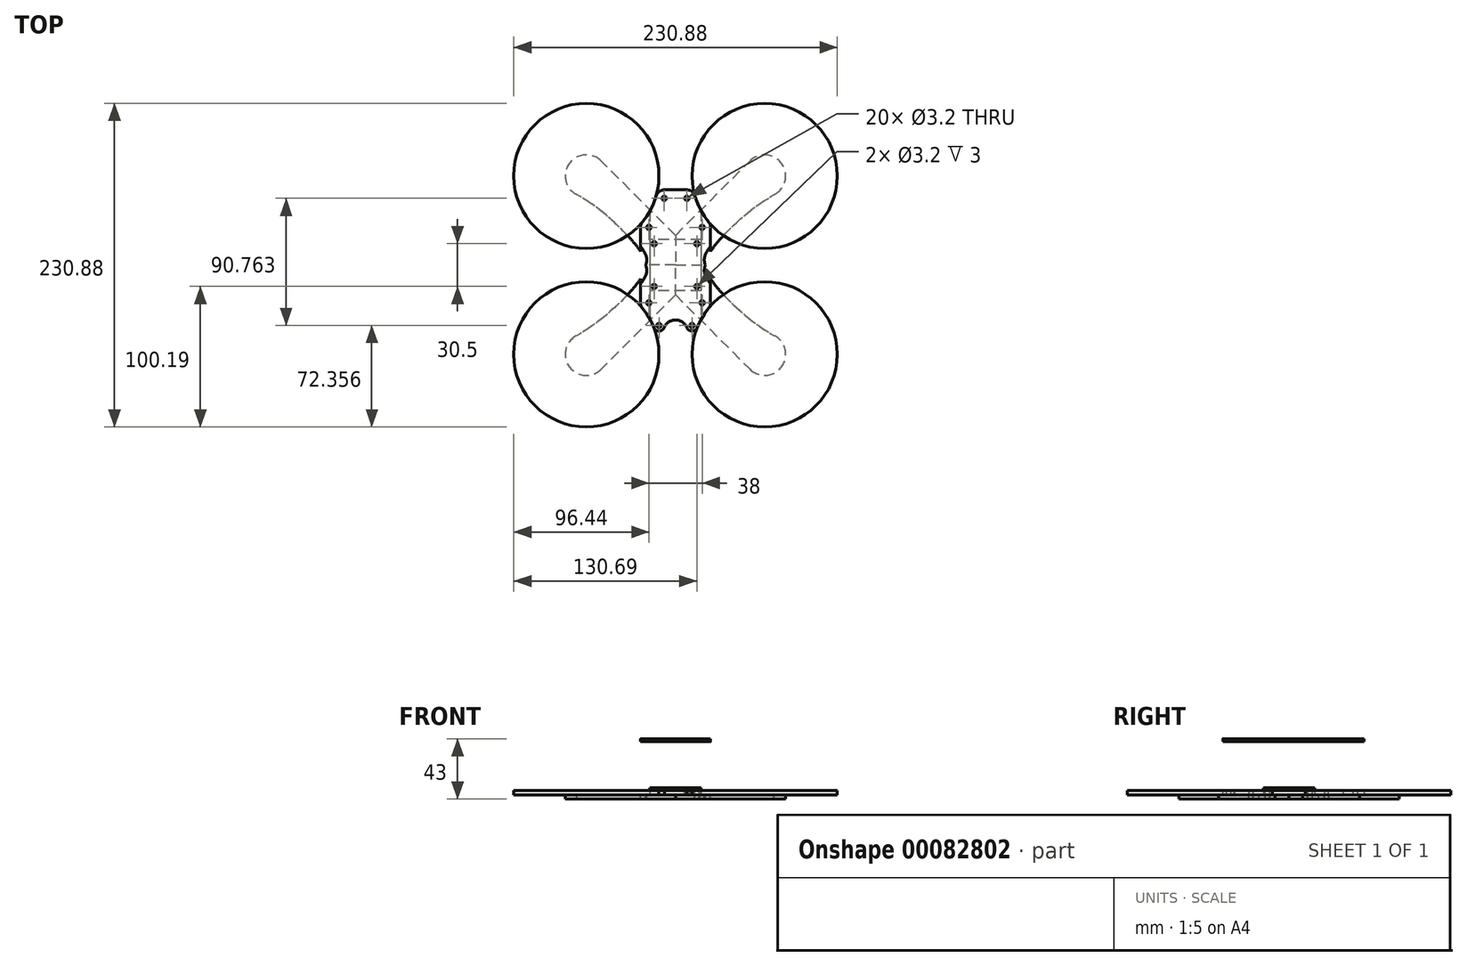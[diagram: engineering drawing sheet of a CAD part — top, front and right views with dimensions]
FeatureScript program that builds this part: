
annotation { "Feature Type Name" : "Feature", "Feature Type Description" : "" }
export const myFeature = defineFeature(function(context is Context, id is Id, definition is map)
    precondition{}
    {
        {
            var Q0;
            Q0=qCreatedBy(makeId("Top.planeOp"),FACE);
            var sketch = newSketch(context, id + "F0", { "sketchPlane" : qUnion([Q0])});
            skLineSegment(sketch, "E0", {"start": v(0, 0) * mm, "end": v(63.64, 63.64) * mm, "construction": true});
            skLineSegment(sketch, "E1", {"start": v(0, 0) * mm, "end": v(77.78, 77.78) * mm, "construction": true});
            skCircle(sketch, "E2", {"center": v(63.64, 63.64) * mm, "radius": 51.8 * mm});
            skCircle(sketch, "E3", {"center": v(77.78, 77.78) * mm, "radius": 64.5 * mm, "construction": true});
            skCircle(sketch, "E4.1.0", {"center": v(-77.78, 77.78) * mm, "radius": 64.5 * mm, "construction": true});
            skCircle(sketch, "E4.1.1", {"center": v(-63.64, 63.64) * mm, "radius": 51.8 * mm});
            skLineSegment(sketch, "E4.1.2", {"start": v(0, 0) * mm, "end": v(-77.78, 77.78) * mm, "construction": true});
            skLineSegment(sketch, "E4.1.3", {"start": v(0, 0) * mm, "end": v(-63.64, 63.64) * mm, "construction": true});
            skCircle(sketch, "E4.2.0", {"center": v(-77.78, -77.78) * mm, "radius": 64.5 * mm, "construction": true});
            skCircle(sketch, "E4.2.1", {"center": v(-63.64, -63.64) * mm, "radius": 51.8 * mm});
            skLineSegment(sketch, "E4.2.2", {"start": v(0, 0) * mm, "end": v(-77.78, -77.78) * mm, "construction": true});
            skLineSegment(sketch, "E4.2.3", {"start": v(0, 0) * mm, "end": v(-63.64, -63.64) * mm, "construction": true});
            skCircle(sketch, "E4.3.0", {"center": v(77.78, -77.78) * mm, "radius": 64.5 * mm, "construction": true});
            skCircle(sketch, "E4.3.1", {"center": v(63.64, -63.64) * mm, "radius": 51.8 * mm});
            skLineSegment(sketch, "E4.3.2", {"start": v(0, 0) * mm, "end": v(77.78, -77.78) * mm, "construction": true});
            skLineSegment(sketch, "E4.3.3", {"start": v(0, 0) * mm, "end": v(63.64, -63.64) * mm, "construction": true});
            skPoint(sketch, "E4.center", {"position": v(0, 0) * mm});
            skLineSegment(sketch, "E5.bottom", {"start": v(18.25, 38.68) * mm, "end": v(-18.25, 38.68) * mm});
            skLineSegment(sketch, "E5.top", {"start": v(18.25, -38.68) * mm, "end": v(-18.25, -38.68) * mm});
            skLineSegment(sketch, "E5.left", {"start": v(18.25, 38.68) * mm, "end": v(18.25, -38.68) * mm});
            skLineSegment(sketch, "E5.right", {"start": v(-18.25, 38.68) * mm, "end": v(-18.25, -38.68) * mm});
            skLineSegment(sketch, "E6.bottom", {"start": v(18.25, 18.25) * mm, "end": v(-18.25, 18.25) * mm});
            skLineSegment(sketch, "E6.top", {"start": v(18.25, -18.25) * mm, "end": v(-18.25, -18.25) * mm});
            skLineSegment(sketch, "E6.left", {"start": v(18.25, 18.25) * mm, "end": v(18.25, -18.25) * mm});
            skLineSegment(sketch, "E6.right", {"start": v(-18.25, 18.25) * mm, "end": v(-18.25, -18.25) * mm});
            skLineSegment(sketch, "E7", {"start": v(-32.57, 53.68) * mm, "end": v(33.13, 53.68) * mm});
            skLineSegment(sketch, "E8", {"start": v(-35.42, -53.68) * mm, "end": v(38.62, -53.68) * mm});
            skLineSegment(sketch, "E9", {"start": v(25, 67.02) * mm, "end": v(25, -83.76) * mm});
            skLineSegment(sketch, "E10.MirrorCS", {"start": v(-25, 67.02) * mm, "end": v(-25, -83.76) * mm});
            skSolve(sketch);
        }
        {
            var Q0;
            {var subQ0=sQuery(id+"F0.wireOp",EDGE,"E5.bottom");Q0=makeQuery(id+"F0.imprint","IMPRINT",FACE,{"disambiguationData":[TD([[makeQuery(id+"F0.imprint","IMPRINT",EDGE,{"derivedFrom":subQ0}),-1.0]])]});}
            var Q1;
            {var subQ0=sQuery(id+"F0.wireOp",EDGE,"E5.bottom");Q1=makeQuery(id+"F0.imprint","IMPRINT",FACE,{"disambiguationData":[TD([[makeQuery(id+"F0.imprint","IMPRINT",EDGE,{"derivedFrom":subQ0}),1.0]])]});}
            var Q2;
            Q2=makeQuery(id+"F0.imprint","IMPRINT",FACE,{"disambiguationData":[TD([[makeQuery(id+"F0.imprint","IMPRINT",EDGE,{"derivedFrom":sQuery(id+"F0.wireOp",EDGE,"E6.bottom")}),1.0]])]});
            var Q3;
            {var subQ0=sQuery(id+"F0.wireOp",EDGE,"E5.top");Q3=makeQuery(id+"F0.imprint","IMPRINT",FACE,{"disambiguationData":[TD([[makeQuery(id+"F0.imprint","IMPRINT",EDGE,{"derivedFrom":subQ0}),-1.0]])]});}
            var Q4;
            {var subQ0=sQuery(id+"F0.wireOp",EDGE,"E5.top");Q4=makeQuery(id+"F0.imprint","IMPRINT",FACE,{"disambiguationData":[TD([[makeQuery(id+"F0.imprint","IMPRINT",EDGE,{"derivedFrom":subQ0}),1.0]])]});}
            var Q5;
            {var subQ5=sQuery(id+"F0.wireOp",EDGE,"E6.right");Q5=makeQuery(id+"F0.imprint","IMPRINT",FACE,{"disambiguationData":[TD([[makeQuery(id+"F0.imprint","IMPRINT",EDGE,{"derivedFrom":subQ5}),-1.0]])]});}
            var Q6;
            {var subQ3=sQuery(id+"F0.wireOp",EDGE,"E6.left");Q6=makeQuery(id+"F0.imprint","IMPRINT",FACE,{"disambiguationData":[TD([[makeQuery(id+"F0.imprint","IMPRINT",EDGE,{"derivedFrom":subQ3}),1.0]])]});}
            extrude(context, id + "F1", {"entities" : qUnion([Q0, Q1, Q2, Q3, Q4, Q5, Q6]), "depth" : 3 * mm});
        }
        {
            var Q0;
            Q0=makeQuery(id+"F0.imprint","IMPRINT",FACE,{"disambiguationData":[TD([[makeQuery(id+"F0.imprint","IMPRINT",EDGE,{"derivedFrom":sQuery(id+"F0.wireOp",EDGE,"E6.bottom")}),1.0]])]});
            extrude(context, id + "F2", {"entities" : qUnion([Q0]), "depth" : 5 * mm});
        }
        {
            var Q0;
            {var subQ0=sQuery(id+"F0.wireOp",EDGE,"E10.MirrorCS");var subQ1=sQuery(id+"F0.wireOp",EDGE,"E4.1.1");var subQ2=makeQuery(id+"F0.imprint","INTERSECT",VERTEX,{"derivedFrom":[subQ1,subQ0]});Q0=makeQuery(id+"F0.imprint","IMPRINT",FACE,{"disambiguationData":[TD([[makeQuery(id+"F0.imprint","IMPRINT",EDGE,{"disambiguationData":[TD([[subQ2,1.0]])],"derivedFrom":subQ1}),1.0]])]});}
            var Q1;
            {var subQ0=sQuery(id+"F0.wireOp",EDGE,"E7");var subQ1=sQuery(id+"F0.wireOp",EDGE,"E2");var subQ2=makeQuery(id+"F0.imprint","INTERSECT",VERTEX,{"derivedFrom":[subQ1,subQ0]});Q1=makeQuery(id+"F0.imprint","IMPRINT",FACE,{"disambiguationData":[TD([[makeQuery(id+"F0.imprint","IMPRINT",EDGE,{"disambiguationData":[TD([[subQ2,1.0]])],"derivedFrom":subQ1}),1.0]])]});}
            var Q2;
            {var subQ0=sQuery(id+"F0.wireOp",EDGE,"E8");var subQ1=sQuery(id+"F0.wireOp",EDGE,"E4.2.1");var subQ2=makeQuery(id+"F0.imprint","INTERSECT",VERTEX,{"derivedFrom":[subQ1,subQ0]});Q2=makeQuery(id+"F0.imprint","IMPRINT",FACE,{"disambiguationData":[TD([[makeQuery(id+"F0.imprint","IMPRINT",EDGE,{"disambiguationData":[TD([[subQ2,1.0]])],"derivedFrom":subQ1}),1.0]])]});}
            var Q3;
            {var subQ0=sQuery(id+"F0.wireOp",EDGE,"E9");var subQ1=sQuery(id+"F0.wireOp",EDGE,"E4.3.1");var subQ2=makeQuery(id+"F0.imprint","INTERSECT",VERTEX,{"derivedFrom":[subQ1,subQ0]});Q3=makeQuery(id+"F0.imprint","IMPRINT",FACE,{"disambiguationData":[TD([[makeQuery(id+"F0.imprint","IMPRINT",EDGE,{"disambiguationData":[TD([[subQ2,1.0]])],"derivedFrom":subQ1}),1.0]])]});}
            var Q4;
            {var subQ2=sQuery(id+"F0.wireOp",EDGE,"E9");var subQ4=sQuery(id+"F0.wireOp",EDGE,"E8");var subQ6=makeQuery(id+"F0.imprint","INTERSECT",VERTEX,{"derivedFrom":[subQ4,subQ2]});Q4=makeQuery(id+"F0.imprint","IMPRINT",FACE,{"disambiguationData":[TD([[makeQuery(id+"F0.imprint","IMPRINT",EDGE,{"disambiguationData":[TD([[subQ6,1.0]])],"derivedFrom":subQ4}),1.0]])]});}
            var Q5;
            {var subQ2=sQuery(id+"F0.wireOp",EDGE,"E8");var subQ4=sQuery(id+"F0.wireOp",EDGE,"E10.MirrorCS");var subQ6=makeQuery(id+"F0.imprint","INTERSECT",VERTEX,{"derivedFrom":[subQ2,subQ4]});Q5=makeQuery(id+"F0.imprint","IMPRINT",FACE,{"disambiguationData":[TD([[makeQuery(id+"F0.imprint","IMPRINT",EDGE,{"disambiguationData":[TD([[subQ6,-1.0]])],"derivedFrom":subQ2}),1.0]])]});}
            var Q6;
            {var subQ2=sQuery(id+"F0.wireOp",EDGE,"E10.MirrorCS");var subQ4=sQuery(id+"F0.wireOp",EDGE,"E7");var subQ6=makeQuery(id+"F0.imprint","INTERSECT",VERTEX,{"derivedFrom":[subQ4,subQ2]});Q6=makeQuery(id+"F0.imprint","IMPRINT",FACE,{"disambiguationData":[TD([[makeQuery(id+"F0.imprint","IMPRINT",EDGE,{"disambiguationData":[TD([[subQ6,-1.0]])],"derivedFrom":subQ4}),-1.0]])]});}
            var Q7;
            {var subQ2=sQuery(id+"F0.wireOp",EDGE,"E7");var subQ4=sQuery(id+"F0.wireOp",EDGE,"E9");var subQ6=makeQuery(id+"F0.imprint","INTERSECT",VERTEX,{"derivedFrom":[subQ2,subQ4]});Q7=makeQuery(id+"F0.imprint","IMPRINT",FACE,{"disambiguationData":[TD([[makeQuery(id+"F0.imprint","IMPRINT",EDGE,{"disambiguationData":[TD([[subQ6,1.0]])],"derivedFrom":subQ2}),-1.0]])]});}
            extrude(context, id + "F3", {"entities" : qUnion([Q0, Q1, Q2, Q3, Q4, Q5, Q6, Q7]), "depth" : 3 * mm});
        }
        {
            var Q0;
            {var subQ0=sQuery(id+"F0.wireOp",EDGE,"E5.bottom");Q0=makeQuery(id+"F0.imprint","IMPRINT",FACE,{"disambiguationData":[TD([[makeQuery(id+"F0.imprint","IMPRINT",EDGE,{"derivedFrom":subQ0}),-1.0]])]});}
            var sketch = newSketch(context, id + "F4", { "sketchPlane" : qUnion([Q0])});
            skArc(sketch, "E11.0.0", {"start": v(-12.8, 53.68) * mm, "mid": v(-17.25, 40.59) * mm, "end": v(-25, 29.14) * mm, "construction": true});
            skLineSegment(sketch, "E11.0.1", {"start": v(-25, 29.14) * mm, "end": v(-25, -29.14) * mm, "construction": true});
            skArc(sketch, "E11.0.2", {"start": v(-25, -29.14) * mm, "mid": v(-17.25, -40.59) * mm, "end": v(-12.8, -53.68) * mm, "construction": true});
            skLineSegment(sketch, "E11.0.3", {"start": v(-12.8, -53.68) * mm, "end": v(12.8, -53.68) * mm, "construction": true});
            skArc(sketch, "E11.0.4", {"start": v(12.8, -53.68) * mm, "mid": v(17.25, -40.59) * mm, "end": v(25, -29.14) * mm, "construction": true});
            skLineSegment(sketch, "E11.0.5", {"start": v(25, -29.14) * mm, "end": v(25, 29.14) * mm, "construction": true});
            skArc(sketch, "E11.0.6", {"start": v(25, 29.14) * mm, "mid": v(17.25, 40.59) * mm, "end": v(12.8, 53.68) * mm, "construction": true});
            skLineSegment(sketch, "E11.0.7", {"start": v(12.8, 53.68) * mm, "end": v(-12.8, 53.68) * mm, "construction": true});
            skCircle(sketch, "E12", {"center": v(63.64, -63.64) * mm, "radius": 15 * mm, "construction": true});
            skLineSegment(sketch, "E13", {"start": v(98.26, -77.05) * mm, "end": v(21.21, 0) * mm});
            skLineSegment(sketch, "E14", {"start": v(0, -21.21) * mm, "end": v(70.57, -91.78) * mm});
            skLineSegment(sketch, "E15", {"start": v(0, -21.21) * mm, "end": v(0, 0) * mm});
            skLineSegment(sketch, "E16", {"start": v(0, 0) * mm, "end": v(21.21, 0) * mm});
            skArc(sketch, "E17", {"start": v(74.25, -53.03) * mm, "mid": v(74.25, -74.25) * mm, "end": v(53.03, -74.25) * mm});
            skSolve(sketch);
        }
        {
            var Q0;
            {var subQ1=sQuery(id+"F4.wireOp",EDGE,"E15");Q0=makeQuery(id+"F4.imprint","IMPRINT",FACE,{"disambiguationData":[TD([[makeQuery(id+"F4.imprint","IMPRINT",EDGE,{"derivedFrom":subQ1}),-1.0]])]});}
            extrude(context, id + "F5", {"entities" : qUnion([Q0]), "oppositeDirection" : true, "depth" : 3 * mm});
        }
        {
            var Q0;
            Q0=makeQuery(id+"F1.opExtrude","SWEPT_EDGE",EDGE,{"disambiguationData":[OSD([sQuery(id+"F0.wireOp",EDGE,"E4.3.1"),sQuery(id+"F0.wireOp",EDGE,"E9")])]});
            var Q1;
            Q1=makeQuery(id+"F1.opExtrude","SWEPT_EDGE",EDGE,{"disambiguationData":[OSD([sQuery(id+"F0.wireOp",EDGE,"E4.3.1"),sQuery(id+"F0.wireOp",EDGE,"E8")])]});
            var Q2;
            Q2=makeQuery(id+"F1.opExtrude","SWEPT_EDGE",EDGE,{"disambiguationData":[OSD([sQuery(id+"F0.wireOp",EDGE,"E2"),sQuery(id+"F0.wireOp",EDGE,"E9")])]});
            var Q3;
            Q3=makeQuery(id+"F1.opExtrude","SWEPT_EDGE",EDGE,{"disambiguationData":[OSD([sQuery(id+"F0.wireOp",EDGE,"E2"),sQuery(id+"F0.wireOp",EDGE,"E7")])]});
            var Q4;
            Q4=makeQuery(id+"F1.opExtrude","SWEPT_EDGE",EDGE,{"disambiguationData":[OSD([sQuery(id+"F0.wireOp",EDGE,"E4.1.1"),sQuery(id+"F0.wireOp",EDGE,"E7")])]});
            var Q5;
            Q5=makeQuery(id+"F1.opExtrude","SWEPT_EDGE",EDGE,{"disambiguationData":[OSD([sQuery(id+"F0.wireOp",EDGE,"E4.1.1"),sQuery(id+"F0.wireOp",EDGE,"E10.MirrorCS")])]});
            var Q6;
            Q6=makeQuery(id+"F1.opExtrude","SWEPT_EDGE",EDGE,{"disambiguationData":[OSD([sQuery(id+"F0.wireOp",EDGE,"E4.2.1"),sQuery(id+"F0.wireOp",EDGE,"E10.MirrorCS")])]});
            var Q7;
            Q7=makeQuery(id+"F1.opExtrude","SWEPT_EDGE",EDGE,{"disambiguationData":[OSD([sQuery(id+"F0.wireOp",EDGE,"E4.2.1"),sQuery(id+"F0.wireOp",EDGE,"E8")])]});
            fillet(context, id + "F6", {"entities" : qUnion([Q0, Q1, Q2, Q3, Q4, Q5, Q6, Q7]), "radius" : 6 * mm, "allowEdgeOverflow" : false});
        }
        {
            var Q0;
            Q0=makeQuery(id+"F5.opExtrude","CAP_FACE",FACE,{"disambiguationData":[OSD([sQuery(id+"F4.wireOp",EDGE,"E13"),sQuery(id+"F4.wireOp",EDGE,"E14"),sQuery(id+"F4.wireOp",EDGE,"E15"),sQuery(id+"F4.wireOp",EDGE,"E16"),sQuery(id+"F4.wireOp",EDGE,"E17")])],"isStart":true});
            var sketch = newSketch(context, id + "F7", { "sketchPlane" : qUnion([Q0])});
            skArc(sketch, "E18.0.0", {"start": v(53.03, -74.25) * mm, "mid": v(74.25, -74.25) * mm, "end": v(74.25, -53.03) * mm});
            skLineSegment(sketch, "E18.0.1", {"start": v(74.25, -53.03) * mm, "end": v(21.21, 0) * mm});
            skLineSegment(sketch, "E18.0.2", {"start": v(21.21, 0) * mm, "end": v(0, 0) * mm});
            skLineSegment(sketch, "E18.0.3", {"start": v(0, 0) * mm, "end": v(0, -21.21) * mm});
            skLineSegment(sketch, "E18.0.4", {"start": v(0, -21.21) * mm, "end": v(53.03, -74.25) * mm});
            skLineSegment(sketch, "E19.0", {"start": v(25, 67.02) * mm, "end": v(25, -83.76) * mm});
            skCircle(sketch, "E20", {"center": v(63.64, -63.64) * mm, "radius": 15 * mm});
            skFitSpline(sketch, "E21", {"points": [v(21.21, 0) * mm, v(40.17, -27.1) * mm, v(70.4, -50.25) * mm], "startDerivative": vector(0, -45.66) * mm, "endDerivative": vector(63.78, -35.61) * mm});
            skArc(sketch, "E22.0.0", {"start": v(23.63, 30.73) * mm, "mid": v(17.8, 39.53) * mm, "end": v(13.85, 49.34) * mm});
            skArc(sketch, "E22.0.1", {"start": v(13.85, 49.34) * mm, "mid": v(11.7, 52.47) * mm, "end": v(8.09, 53.68) * mm});
            skLineSegment(sketch, "E22.0.2", {"start": v(8.09, 53.68) * mm, "end": v(-8.09, 53.68) * mm});
            skArc(sketch, "E22.0.3", {"start": v(-8.09, 53.68) * mm, "mid": v(-11.7, 52.47) * mm, "end": v(-13.85, 49.34) * mm});
            skArc(sketch, "E22.0.4", {"start": v(-13.85, 49.34) * mm, "mid": v(-17.8, 39.53) * mm, "end": v(-23.63, 30.73) * mm});
            skArc(sketch, "E22.0.5", {"start": v(-23.63, 30.73) * mm, "mid": v(-24.65, 28.95) * mm, "end": v(-25, 26.92) * mm});
            skLineSegment(sketch, "E22.0.6", {"start": v(-25, 26.92) * mm, "end": v(-25, -26.92) * mm});
            skArc(sketch, "E22.0.7", {"start": v(-25, -26.92) * mm, "mid": v(-24.65, -28.95) * mm, "end": v(-23.63, -30.73) * mm});
            skArc(sketch, "E22.0.8", {"start": v(-23.63, -30.73) * mm, "mid": v(-17.8, -39.53) * mm, "end": v(-13.85, -49.34) * mm});
            skArc(sketch, "E22.0.9", {"start": v(-13.85, -49.34) * mm, "mid": v(-11.7, -52.47) * mm, "end": v(-8.09, -53.68) * mm});
            skLineSegment(sketch, "E22.0.10", {"start": v(-8.09, -53.68) * mm, "end": v(8.09, -53.68) * mm});
            skArc(sketch, "E22.0.11", {"start": v(8.09, -53.68) * mm, "mid": v(11.7, -52.47) * mm, "end": v(13.85, -49.34) * mm});
            skArc(sketch, "E22.0.12", {"start": v(13.85, -49.34) * mm, "mid": v(17.8, -39.53) * mm, "end": v(23.63, -30.73) * mm});
            skArc(sketch, "E22.0.13", {"start": v(23.63, -30.73) * mm, "mid": v(24.65, -28.95) * mm, "end": v(25, -26.92) * mm});
            skLineSegment(sketch, "E22.0.14", {"start": v(25, -26.92) * mm, "end": v(25, 26.92) * mm});
            skArc(sketch, "E22.0.15", {"start": v(25, 26.92) * mm, "mid": v(24.65, 28.95) * mm, "end": v(23.63, 30.73) * mm});
            skSolve(sketch);
        }
        {
            var Q0;
            {var subQ0=sQuery(id+"F7.wireOp",EDGE,"E20");var subQ1=sQuery(id+"F7.wireOp",EDGE,"E18.0.1");var subQ2=makeQuery(id+"F7.imprint","INTERSECT",VERTEX,{"derivedFrom":[subQ1,subQ0]});Q0=makeQuery(id+"F7.imprint","IMPRINT",FACE,{"disambiguationData":[TD([[makeQuery(id+"F7.imprint","IMPRINT",EDGE,{"disambiguationData":[TD([[subQ2,-1.0]])],"derivedFrom":subQ1}),1.0]])]});}
            var Q1;
            {var subQ1=sQuery(id+"F7.wireOp",EDGE,"E18.0.1");var subQ3=sQuery(id+"F7.wireOp",EDGE,"E22.0.14");var subQ4=makeQuery(id+"F7.imprint","INTERSECT",VERTEX,{"derivedFrom":[subQ1,subQ3]});Q1=makeQuery(id+"F7.imprint","IMPRINT",FACE,{"disambiguationData":[TD([[makeQuery(id+"F7.imprint","IMPRINT",EDGE,{"disambiguationData":[TD([[subQ4,1.0]])],"derivedFrom":subQ3}),1.0]])]});}
            extrude(context, id + "F8", {"entities" : qUnion([Q0, Q1]), "operationType" : NewBodyOperationType.REMOVE, "endBound" : BoundingType.THROUGH_ALL, "oppositeDirection" : true, "depth" : 25 * mm});
        }
        {
            var Q0;
            Q0=makeQuery(id+"F5.opExtrude","SWEPT_BODY",BODY,{"disambiguationData":[OSD([sQuery(id+"F4.wireOp",EDGE,"E13"),sQuery(id+"F4.wireOp",EDGE,"E14"),sQuery(id+"F4.wireOp",EDGE,"E15"),sQuery(id+"F4.wireOp",EDGE,"E16"),sQuery(id+"F4.wireOp",EDGE,"E17")])]});
            var Q1;
            Q1=makeQuery(id+"F5.opExtrude","SWEPT_EDGE",EDGE,{"disambiguationData":[OSD([sQuery(id+"F4.wireOp",EDGE,"E15"),sQuery(id+"F4.wireOp",EDGE,"E16")])]});
            circularPattern(context, id + "F9", {"entities" : qUnion([Q0]), "axis" : qUnion([Q1]), "angle" : 180 * degree, "instanceCount" : 2});
        }
        {
            var Q0;
            Q0=makeQuery(id+"F9.opPattern","COPY",BODY,{"derivedFrom":makeQuery(id+"F5.opExtrude","SWEPT_BODY",BODY,{"disambiguationData":[OSD([sQuery(id+"F4.wireOp",EDGE,"E13"),sQuery(id+"F4.wireOp",EDGE,"E14"),sQuery(id+"F4.wireOp",EDGE,"E15"),sQuery(id+"F4.wireOp",EDGE,"E16"),sQuery(id+"F4.wireOp",EDGE,"E17")])]}),"instanceName":"1"});
            var Q1;
            Q1=makeQuery(id+"F5.opExtrude","SWEPT_BODY",BODY,{"disambiguationData":[OSD([sQuery(id+"F4.wireOp",EDGE,"E13"),sQuery(id+"F4.wireOp",EDGE,"E14"),sQuery(id+"F4.wireOp",EDGE,"E15"),sQuery(id+"F4.wireOp",EDGE,"E16"),sQuery(id+"F4.wireOp",EDGE,"E17")])]});
            var Q2;
            Q2=qCreatedBy(makeId("Right.planeOp"),FACE);
            mirror(context, id + "F10", {"entities" : qUnion([Q0, Q1]), "mirrorPlane" : qUnion([Q2])});
        }
        {
            var Q0;
            Q0=makeQuery(id+"F1.opExtrude","CAP_FACE",FACE,{"disambiguationData":[OSD([sQuery(id+"F0.wireOp",EDGE,"E2"),sQuery(id+"F0.wireOp",EDGE,"E4.1.1"),sQuery(id+"F0.wireOp",EDGE,"E4.2.1"),sQuery(id+"F0.wireOp",EDGE,"E4.3.1"),sQuery(id+"F0.wireOp",EDGE,"E7"),sQuery(id+"F0.wireOp",EDGE,"E8"),sQuery(id+"F0.wireOp",EDGE,"E9"),sQuery(id+"F0.wireOp",EDGE,"E10.MirrorCS")])],"isStart":false});
            var sketch = newSketch(context, id + "F11", { "sketchPlane" : qUnion([Q0])});
            skFitSpline(sketch, "E23.0", {"points": [v(21.21, 0) * mm, v(21.21, -7.34) * mm, v(41.38, -29.78) * mm, v(59.4, -44.1) * mm, v(70.4, -50.25) * mm]});
            skFitSpline(sketch, "E24.0", {"points": [v(21.21, 0) * mm, v(21.21, 7.34) * mm, v(41.38, 29.78) * mm, v(59.4, 44.1) * mm, v(70.4, 50.25) * mm]});
            skLineSegment(sketch, "E25.0", {"start": v(25, 26.92) * mm, "end": v(25, -26.92) * mm});
            skFitSpline(sketch, "E26.0", {"points": [v(-21.21, 0) * mm, v(-21.21, 7.34) * mm, v(-41.38, 29.78) * mm, v(-59.4, 44.1) * mm, v(-70.4, 50.25) * mm]});
            skLineSegment(sketch, "E27.0", {"start": v(-25, 26.92) * mm, "end": v(-25, -26.92) * mm});
            skFitSpline(sketch, "E28.0", {"points": [v(-21.21, 0) * mm, v(-21.21, -7.34) * mm, v(-41.38, -29.78) * mm, v(-59.4, -44.1) * mm, v(-70.4, -50.25) * mm]});
            skSolve(sketch);
        }
        {
            var Q0;
            {var subQ0=sQuery(id+"F11.wireOp",EDGE,"E28.0");var subQ1=sQuery(id+"F11.wireOp",EDGE,"E26.0");var subQ2=makeQuery(id+"F11.imprint","INTERSECT",VERTEX,{"derivedFrom":[subQ1,subQ0]});Q0=makeQuery(id+"F11.imprint","IMPRINT",FACE,{"disambiguationData":[TD([[makeQuery(id+"F11.imprint","IMPRINT",EDGE,{"disambiguationData":[TD([[subQ2,-1.0]])],"derivedFrom":subQ1}),1.0]])]});}
            var Q1;
            {var subQ0=sQuery(id+"F11.wireOp",EDGE,"E24.0");var subQ1=sQuery(id+"F11.wireOp",EDGE,"E23.0");var subQ2=makeQuery(id+"F11.imprint","INTERSECT",VERTEX,{"derivedFrom":[subQ1,subQ0]});Q1=makeQuery(id+"F11.imprint","IMPRINT",FACE,{"disambiguationData":[TD([[makeQuery(id+"F11.imprint","IMPRINT",EDGE,{"disambiguationData":[TD([[subQ2,-1.0]])],"derivedFrom":subQ1}),1.0]])]});}
            extrude(context, id + "F12", {"entities" : qUnion([Q0, Q1]), "operationType" : NewBodyOperationType.REMOVE, "endBound" : BoundingType.THROUGH_ALL, "oppositeDirection" : true, "depth" : 25 * mm});
        }
        {
            var Q0;
            Q0=makeQuery(id+"F1.opExtrude","CAP_FACE",FACE,{"disambiguationData":[OSD([sQuery(id+"F0.wireOp",EDGE,"E2"),sQuery(id+"F0.wireOp",EDGE,"E4.1.1"),sQuery(id+"F0.wireOp",EDGE,"E4.2.1"),sQuery(id+"F0.wireOp",EDGE,"E4.3.1"),sQuery(id+"F0.wireOp",EDGE,"E7"),sQuery(id+"F0.wireOp",EDGE,"E8"),sQuery(id+"F0.wireOp",EDGE,"E9"),sQuery(id+"F0.wireOp",EDGE,"E10.MirrorCS")])],"isStart":false});
            cPlane(context, id + "F13", {"entities" : qUnion([Q0]), "cplaneType" : CPlaneType.OFFSET, "offset" : 35 * mm, "width" : 150 * mm, "height" : 150 * mm});
        }
        {
            var Q0;
            Q0=makeQuery(id+"F1.opExtrude","CAP_FACE",FACE,{"disambiguationData":[OSD([sQuery(id+"F0.wireOp",EDGE,"E2"),sQuery(id+"F0.wireOp",EDGE,"E4.1.1"),sQuery(id+"F0.wireOp",EDGE,"E4.2.1"),sQuery(id+"F0.wireOp",EDGE,"E4.3.1"),sQuery(id+"F0.wireOp",EDGE,"E7"),sQuery(id+"F0.wireOp",EDGE,"E8"),sQuery(id+"F0.wireOp",EDGE,"E9"),sQuery(id+"F0.wireOp",EDGE,"E10.MirrorCS")])],"isStart":false});
            var sketch = newSketch(context, id + "F14", { "sketchPlane" : qUnion([Q0])});
            skFitSpline(sketch, "E29.0.0", {"points": [v(70.4, -50.25) * mm, v(59.4, -44.1) * mm, v(41.38, -29.78) * mm, v(21.21, -7.34) * mm, v(21.21, 0) * mm], "construction": true});
            skFitSpline(sketch, "E29.0.1", {"points": [v(21.21, 0) * mm, v(21.21, 7.34) * mm, v(41.38, 29.78) * mm, v(59.4, 44.1) * mm, v(70.4, 50.25) * mm], "construction": true});
            skLineSegment(sketch, "E29.0.2", {"start": v(25, 9.8) * mm, "end": v(25, 26.92) * mm, "construction": true});
            skArc(sketch, "E29.0.3", {"start": v(25, 26.92) * mm, "mid": v(24.65, 28.95) * mm, "end": v(23.63, 30.73) * mm, "construction": true});
            skArc(sketch, "E29.0.4", {"start": v(23.63, 30.73) * mm, "mid": v(17.8, 39.53) * mm, "end": v(13.85, 49.34) * mm, "construction": true});
            skArc(sketch, "E29.0.5", {"start": v(13.85, 49.34) * mm, "mid": v(11.7, 52.47) * mm, "end": v(8.09, 53.68) * mm, "construction": true});
            skLineSegment(sketch, "E29.0.6", {"start": v(8.09, 53.68) * mm, "end": v(-8.09, 53.68) * mm, "construction": true});
            skArc(sketch, "E29.0.7", {"start": v(-8.09, 53.68) * mm, "mid": v(-11.7, 52.47) * mm, "end": v(-13.85, 49.34) * mm, "construction": true});
            skArc(sketch, "E29.0.8", {"start": v(-13.85, 49.34) * mm, "mid": v(-17.8, 39.53) * mm, "end": v(-23.63, 30.73) * mm, "construction": true});
            skArc(sketch, "E29.0.9", {"start": v(-23.63, 30.73) * mm, "mid": v(-24.65, 28.95) * mm, "end": v(-25, 26.92) * mm, "construction": true});
            skLineSegment(sketch, "E29.0.10", {"start": v(-25, 26.92) * mm, "end": v(-25, 9.8) * mm, "construction": true});
            skFitSpline(sketch, "E29.0.11", {"points": [v(-70.4, 50.25) * mm, v(-59.4, 44.1) * mm, v(-41.38, 29.78) * mm, v(-21.21, 7.34) * mm, v(-21.21, 0) * mm], "construction": true});
            skFitSpline(sketch, "E29.0.12", {"points": [v(-21.21, 0) * mm, v(-21.21, -7.34) * mm, v(-41.38, -29.78) * mm, v(-59.4, -44.1) * mm, v(-70.4, -50.25) * mm], "construction": true});
            skLineSegment(sketch, "E29.0.13", {"start": v(-25, -9.8) * mm, "end": v(-25, -26.92) * mm, "construction": true});
            skArc(sketch, "E29.0.14", {"start": v(-25, -26.92) * mm, "mid": v(-24.65, -28.95) * mm, "end": v(-23.63, -30.73) * mm, "construction": true});
            skArc(sketch, "E29.0.15", {"start": v(-23.63, -30.73) * mm, "mid": v(-17.8, -39.53) * mm, "end": v(-13.85, -49.34) * mm, "construction": true});
            skArc(sketch, "E29.0.16", {"start": v(-13.85, -49.34) * mm, "mid": v(-11.7, -52.47) * mm, "end": v(-8.09, -53.68) * mm, "construction": true});
            skLineSegment(sketch, "E29.0.17", {"start": v(-8.09, -53.68) * mm, "end": v(8.09, -53.68) * mm, "construction": true});
            skArc(sketch, "E29.0.18", {"start": v(8.09, -53.68) * mm, "mid": v(11.7, -52.47) * mm, "end": v(13.85, -49.34) * mm, "construction": true});
            skArc(sketch, "E29.0.19", {"start": v(13.85, -49.34) * mm, "mid": v(17.8, -39.53) * mm, "end": v(23.63, -30.73) * mm, "construction": true});
            skArc(sketch, "E29.0.20", {"start": v(23.63, -30.73) * mm, "mid": v(24.65, -28.95) * mm, "end": v(25, -26.92) * mm, "construction": true});
            skLineSegment(sketch, "E29.0.21", {"start": v(25, -26.92) * mm, "end": v(25, -9.8) * mm, "construction": true});
            skCircle(sketch, "E30", {"center": v(19, 26.92) * mm, "radius": 1.6 * mm});
            skCircle(sketch, "E31", {"center": v(19, -26.92) * mm, "radius": 1.6 * mm});
            skCircle(sketch, "E32", {"center": v(8.09, 47.68) * mm, "radius": 1.6 * mm});
            skCircle(sketch, "E33", {"center": v(15.25, 15.25) * mm, "radius": 1.6 * mm});
            skCircle(sketch, "E34", {"center": v(15.25, -15.25) * mm, "radius": 1.6 * mm});
            skCircle(sketch, "E35", {"center": v(11.76, -43.08) * mm, "radius": 1.6 * mm});
            skSolve(sketch);
        }
        {
            var Q0;
            Q0 = qSketchRegion(id + "F14", true);
            extrude(context, id + "F15", {"entities" : qUnion([Q0]), "operationType" : NewBodyOperationType.REMOVE, "endBound" : BoundingType.THROUGH_ALL, "oppositeDirection" : true, "depth" : 25 * mm});
        }
        {
            var Q0;
            Q0=qCreatedBy(id+"F13.planeOp",FACE);
            var sketch = newSketch(context, id + "F16", { "sketchPlane" : qUnion([Q0])});
            skFitSpline(sketch, "E36.0.0", {"points": [v(70.4, -50.25) * mm, v(59.4, -44.1) * mm, v(41.38, -29.78) * mm, v(21.21, -7.34) * mm, v(21.21, 0) * mm]});
            skFitSpline(sketch, "E36.0.1", {"points": [v(21.21, 0) * mm, v(21.21, 7.34) * mm, v(41.38, 29.78) * mm, v(59.4, 44.1) * mm, v(70.4, 50.25) * mm]});
            skLineSegment(sketch, "E36.0.2", {"start": v(25, 9.8) * mm, "end": v(25, 26.92) * mm});
            skArc(sketch, "E36.0.3", {"start": v(25, 26.92) * mm, "mid": v(24.65, 28.95) * mm, "end": v(23.63, 30.73) * mm});
            skArc(sketch, "E36.0.4", {"start": v(23.63, 30.73) * mm, "mid": v(17.8, 39.53) * mm, "end": v(13.85, 49.34) * mm});
            skArc(sketch, "E36.0.5", {"start": v(13.85, 49.34) * mm, "mid": v(11.7, 52.47) * mm, "end": v(8.09, 53.68) * mm});
            skLineSegment(sketch, "E36.0.6", {"start": v(8.09, 53.68) * mm, "end": v(-8.09, 53.68) * mm});
            skArc(sketch, "E36.0.7", {"start": v(-8.09, 53.68) * mm, "mid": v(-11.7, 52.47) * mm, "end": v(-13.85, 49.34) * mm});
            skArc(sketch, "E36.0.8", {"start": v(-13.85, 49.34) * mm, "mid": v(-17.8, 39.53) * mm, "end": v(-23.63, 30.73) * mm});
            skArc(sketch, "E36.0.9", {"start": v(-23.63, 30.73) * mm, "mid": v(-24.65, 28.95) * mm, "end": v(-25, 26.92) * mm});
            skLineSegment(sketch, "E36.0.10", {"start": v(-25, 26.92) * mm, "end": v(-25, 9.8) * mm});
            skFitSpline(sketch, "E36.0.11", {"points": [v(-70.4, 50.25) * mm, v(-59.4, 44.1) * mm, v(-41.38, 29.78) * mm, v(-21.21, 7.34) * mm, v(-21.21, 0) * mm]});
            skFitSpline(sketch, "E36.0.12", {"points": [v(-21.21, 0) * mm, v(-21.21, -7.34) * mm, v(-41.38, -29.78) * mm, v(-59.4, -44.1) * mm, v(-70.4, -50.25) * mm]});
            skLineSegment(sketch, "E36.0.13", {"start": v(-25, -9.8) * mm, "end": v(-25, -26.92) * mm});
            skArc(sketch, "E36.0.14", {"start": v(-25, -26.92) * mm, "mid": v(-24.65, -28.95) * mm, "end": v(-23.63, -30.73) * mm});
            skArc(sketch, "E36.0.15", {"start": v(-23.63, -30.73) * mm, "mid": v(-17.8, -39.53) * mm, "end": v(-13.85, -49.34) * mm});
            skArc(sketch, "E36.0.16", {"start": v(-13.85, -49.34) * mm, "mid": v(-11.7, -52.47) * mm, "end": v(-8.09, -53.68) * mm});
            skLineSegment(sketch, "E36.0.17", {"start": v(-8.09, -53.68) * mm, "end": v(8.09, -53.68) * mm});
            skArc(sketch, "E36.0.18", {"start": v(8.09, -53.68) * mm, "mid": v(11.7, -52.47) * mm, "end": v(13.85, -49.34) * mm});
            skArc(sketch, "E36.0.19", {"start": v(13.85, -49.34) * mm, "mid": v(17.8, -39.53) * mm, "end": v(23.63, -30.73) * mm});
            skArc(sketch, "E36.0.20", {"start": v(23.63, -30.73) * mm, "mid": v(24.65, -28.95) * mm, "end": v(25, -26.92) * mm});
            skLineSegment(sketch, "E36.0.21", {"start": v(25, -26.92) * mm, "end": v(25, -9.8) * mm});
            skCircle(sketch, "E37.0", {"center": v(-8.09, 47.68) * mm, "radius": 1.6 * mm});
            skCircle(sketch, "E38.0", {"center": v(8.09, 47.68) * mm, "radius": 1.6 * mm});
            skCircle(sketch, "E39.0", {"center": v(-19, 26.92) * mm, "radius": 1.6 * mm});
            skCircle(sketch, "E40.0", {"center": v(19, 26.92) * mm, "radius": 1.6 * mm});
            skCircle(sketch, "E41.0", {"center": v(15.25, 15.25) * mm, "radius": 1.6 * mm});
            skCircle(sketch, "E42.0", {"center": v(-15.25, 15.25) * mm, "radius": 1.6 * mm});
            skCircle(sketch, "E43.0", {"center": v(-15.25, -15.25) * mm, "radius": 1.6 * mm});
            skCircle(sketch, "E44.0", {"center": v(15.25, -15.25) * mm, "radius": 1.6 * mm});
            skCircle(sketch, "E45.0", {"center": v(19, -26.92) * mm, "radius": 1.6 * mm});
            skCircle(sketch, "E46.0", {"center": v(11.76, -43.08) * mm, "radius": 1.6 * mm});
            skCircle(sketch, "E47.0", {"center": v(-11.76, -43.08) * mm, "radius": 1.6 * mm});
            skCircle(sketch, "E48.0", {"center": v(-19, -26.92) * mm, "radius": 1.6 * mm});
            skSolve(sketch);
        }
        {
            var Q0;
            Q0=makeQuery(id+"F16.imprint","IMPRINT",FACE,{"disambiguationData":[TD([[makeQuery(id+"F16.imprint","IMPRINT",EDGE,{"derivedFrom":sQuery(id+"F16.wireOp",EDGE,"E36.0.0")}),1.0]])]});
            extrude(context, id + "F17", {"entities" : qUnion([Q0]), "depth" : 2 * mm});
        }
        {
            var Q0;
            Q0=makeQuery(id+"F3.opExtrude","CAP_FACE",FACE,{"disambiguationData":[OSD([sQuery(id+"F0.wireOp",EDGE,"E4.3.1")])],"isStart":false});
            var sketch = newSketch(context, id + "F18", { "sketchPlane" : qUnion([Q0])});
            skLineSegment(sketch, "E49.0.0", {"start": v(25, -26.92) * mm, "end": v(25, -9.8) * mm});
            skFitSpline(sketch, "E49.0.1", {"points": [v(70.4, -50.25) * mm, v(59.4, -44.1) * mm, v(41.38, -29.78) * mm, v(21.21, -7.34) * mm, v(21.21, 0) * mm]});
            skFitSpline(sketch, "E49.0.2", {"points": [v(21.21, 0) * mm, v(21.21, 7.34) * mm, v(41.38, 29.78) * mm, v(59.4, 44.1) * mm, v(70.4, 50.25) * mm]});
            skLineSegment(sketch, "E49.0.3", {"start": v(25, 9.8) * mm, "end": v(25, 26.92) * mm});
            skArc(sketch, "E49.0.4", {"start": v(25, 26.92) * mm, "mid": v(24.65, 28.95) * mm, "end": v(23.63, 30.73) * mm});
            skArc(sketch, "E49.0.5", {"start": v(23.63, 30.73) * mm, "mid": v(17.8, 39.53) * mm, "end": v(13.85, 49.34) * mm});
            skArc(sketch, "E49.0.6", {"start": v(13.85, 49.34) * mm, "mid": v(11.7, 52.47) * mm, "end": v(8.09, 53.68) * mm});
            skLineSegment(sketch, "E49.0.7", {"start": v(8.09, 53.68) * mm, "end": v(-8.09, 53.68) * mm});
            skArc(sketch, "E49.0.8", {"start": v(-8.09, 53.68) * mm, "mid": v(-11.7, 52.47) * mm, "end": v(-13.85, 49.34) * mm});
            skArc(sketch, "E49.0.9", {"start": v(-13.85, 49.34) * mm, "mid": v(-17.8, 39.53) * mm, "end": v(-23.63, 30.73) * mm});
            skArc(sketch, "E49.0.10", {"start": v(-23.63, 30.73) * mm, "mid": v(-24.65, 28.95) * mm, "end": v(-25, 26.92) * mm});
            skLineSegment(sketch, "E49.0.11", {"start": v(-25, 26.92) * mm, "end": v(-25, 9.8) * mm});
            skFitSpline(sketch, "E49.0.12", {"points": [v(-70.4, 50.25) * mm, v(-59.4, 44.1) * mm, v(-41.38, 29.78) * mm, v(-21.21, 7.34) * mm, v(-21.21, 0) * mm]});
            skFitSpline(sketch, "E49.0.13", {"points": [v(-21.21, 0) * mm, v(-21.21, -7.34) * mm, v(-41.38, -29.78) * mm, v(-59.4, -44.1) * mm, v(-70.4, -50.25) * mm]});
            skLineSegment(sketch, "E49.0.14", {"start": v(-25, -9.8) * mm, "end": v(-25, -26.92) * mm});
            skArc(sketch, "E49.0.15", {"start": v(-25, -26.92) * mm, "mid": v(-24.65, -28.95) * mm, "end": v(-23.63, -30.73) * mm});
            skArc(sketch, "E49.0.16", {"start": v(-23.63, -30.73) * mm, "mid": v(-17.8, -39.53) * mm, "end": v(-13.85, -49.34) * mm});
            skArc(sketch, "E49.0.17", {"start": v(-13.85, -49.34) * mm, "mid": v(-11.7, -52.47) * mm, "end": v(-8.09, -53.68) * mm});
            skLineSegment(sketch, "E49.0.18", {"start": v(-8.09, -53.68) * mm, "end": v(8.09, -53.68) * mm});
            skArc(sketch, "E49.0.19", {"start": v(8.09, -53.68) * mm, "mid": v(11.7, -52.47) * mm, "end": v(13.85, -49.34) * mm});
            skArc(sketch, "E49.0.20", {"start": v(13.85, -49.34) * mm, "mid": v(17.8, -39.53) * mm, "end": v(23.63, -30.73) * mm});
            skArc(sketch, "E49.0.21", {"start": v(23.63, -30.73) * mm, "mid": v(24.65, -28.95) * mm, "end": v(25, -26.92) * mm});
            skCircle(sketch, "E50.0", {"center": v(-11.76, -43.08) * mm, "radius": 1.6 * mm});
            skCircle(sketch, "E51.0", {"center": v(11.76, -43.08) * mm, "radius": 1.6 * mm});
            skCircle(sketch, "E52", {"center": v(-11.76, -43.08) * mm, "radius": 4 * mm});
            skCircle(sketch, "E53", {"center": v(11.76, -43.08) * mm, "radius": 4 * mm});
            skArc(sketch, "E54", {"start": v(8, -44.43) * mm, "mid": v(0, -39.16) * mm, "end": v(-8, -44.43) * mm});
            skSolve(sketch);
        }
        {
            var Q0;
            Q0=makeQuery(id+"F17.opExtrude","CAP_FACE",FACE,{"disambiguationData":[OSD([sQuery(id+"F16.wireOp",EDGE,"E36.0.0"),sQuery(id+"F16.wireOp",EDGE,"E36.0.1"),sQuery(id+"F16.wireOp",EDGE,"E36.0.2"),sQuery(id+"F16.wireOp",EDGE,"E36.0.3"),sQuery(id+"F16.wireOp",EDGE,"E36.0.4"),sQuery(id+"F16.wireOp",EDGE,"E36.0.5"),sQuery(id+"F16.wireOp",EDGE,"E36.0.6"),sQuery(id+"F16.wireOp",EDGE,"E36.0.7"),sQuery(id+"F16.wireOp",EDGE,"E36.0.8"),sQuery(id+"F16.wireOp",EDGE,"E36.0.9"),sQuery(id+"F16.wireOp",EDGE,"E36.0.10"),sQuery(id+"F16.wireOp",EDGE,"E36.0.11"),sQuery(id+"F16.wireOp",EDGE,"E36.0.12"),sQuery(id+"F16.wireOp",EDGE,"E36.0.13"),sQuery(id+"F16.wireOp",EDGE,"E36.0.14"),sQuery(id+"F16.wireOp",EDGE,"E36.0.15"),sQuery(id+"F16.wireOp",EDGE,"E36.0.16"),sQuery(id+"F16.wireOp",EDGE,"E36.0.17"),sQuery(id+"F16.wireOp",EDGE,"E36.0.18"),sQuery(id+"F16.wireOp",EDGE,"E36.0.19"),sQuery(id+"F16.wireOp",EDGE,"E36.0.20"),sQuery(id+"F16.wireOp",EDGE,"E36.0.21"),sQuery(id+"F16.wireOp",EDGE,"E37.0"),sQuery(id+"F16.wireOp",EDGE,"E38.0"),sQuery(id+"F16.wireOp",EDGE,"E39.0"),sQuery(id+"F16.wireOp",EDGE,"E40.0"),sQuery(id+"F16.wireOp",EDGE,"E41.0"),sQuery(id+"F16.wireOp",EDGE,"E42.0"),sQuery(id+"F16.wireOp",EDGE,"E44.0"),sQuery(id+"F16.wireOp",EDGE,"E45.0"),sQuery(id+"F16.wireOp",EDGE,"E46.0"),sQuery(id+"F16.wireOp",EDGE,"E47.0"),sQuery(id+"F16.wireOp",EDGE,"E48.0"),sQuery(id+"F16.wireOp",EDGE,"E43.0")])],"isStart":false});
            var sketch = newSketch(context, id + "F19", { "sketchPlane" : qUnion([Q0])});
            skArc(sketch, "E55.0", {"start": v(-23.63, -30.73) * mm, "mid": v(-17.8, -39.53) * mm, "end": v(-13.85, -49.34) * mm});
            skCircle(sketch, "E56.0", {"center": v(-11.76, -43.08) * mm, "radius": 4 * mm});
            skArc(sketch, "E57.0", {"start": v(8, -44.43) * mm, "mid": v(0, -39.16) * mm, "end": v(-8, -44.43) * mm});
            skCircle(sketch, "E58.0", {"center": v(11.76, -43.08) * mm, "radius": 4 * mm});
            skArc(sketch, "E59.0", {"start": v(13.85, -49.34) * mm, "mid": v(17.8, -39.53) * mm, "end": v(23.63, -30.73) * mm});
            skArc(sketch, "E60.0", {"start": v(8.09, -53.68) * mm, "mid": v(11.7, -52.47) * mm, "end": v(13.85, -49.34) * mm});
            skLineSegment(sketch, "E61.0", {"start": v(-8.09, -53.68) * mm, "end": v(8.09, -53.68) * mm});
            skArc(sketch, "E62.0", {"start": v(-13.85, -49.34) * mm, "mid": v(-11.7, -52.47) * mm, "end": v(-8.09, -53.68) * mm});
            skSolve(sketch);
        }
        {
            var Q0;
            {var subQ0=sQuery(id+"F19.wireOp",EDGE,"E57.0");Q0=makeQuery(id+"F19.imprint","IMPRINT",FACE,{"disambiguationData":[TD([[makeQuery(id+"F19.imprint","IMPRINT",EDGE,{"derivedFrom":subQ0}),1.0]])]});}
            extrude(context, id + "F20", {"entities" : qUnion([Q0]), "operationType" : NewBodyOperationType.REMOVE, "endBound" : BoundingType.THROUGH_ALL, "oppositeDirection" : true, "depth" : 25 * mm});
        }
    });
